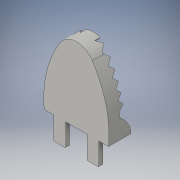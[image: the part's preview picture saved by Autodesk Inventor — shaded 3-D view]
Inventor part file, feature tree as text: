
AUTODESK INVENTOR PART (.ipt)
format: ipt  version: 2016 (Build 200138000, 138)  size: 525,824 bytes
history: native  units: in
note: dims shown in document units (in); Inventor stores cm internally (conversion verified against a paired STEP export)
features: sketch x25, extrude x24, other x12, plane x12, projected_geometry x8, reference x4, fillet x3
ambient origin geometry x8: Origin, YZ Plane, XZ Plane, XY Plane, X Axis, Y Axis, Z Axis, Center Point
bodies: Solid1 (feature_tree)
feature tree (88):
  extrude  "Extrusion1"  Depth=1.0in
  extrude  "Extrusion2"  Depth=0.3937in TaperAngle=0.0deg
  extrude  "Extrusion3"  Depth=1.0in
  extrude  "Extrusion4"  Depth=1.0in TaperAngle=0.0deg
  sketch  "Sketch5"  dims[d12=1.0in d13=0.0in d15=0.5in]
  other  "Work Point1"
  other  "Work Point2"
  other  "Work Point3"
  other  "Work Point4"
  other  "Work Point5"
  other  "Work Point6"
  other  "Work Point7"
  other  "Work Point8"
  other  "Work Point9"
  other  "Work Point10"
  other  "Work Point11"
  other  "Work Point12"
  plane  "Work Plane1"
  plane  "Work Plane2"
  plane  "Work Plane3"
  plane  "Work Plane4"
  plane  "Work Plane5"
  plane  "Work Plane6"
  sketch  "Sketch6"  dims[d16=2.3622in d18=0.45in d19=0.3937in d21=1.0in d23=0.25in]
  sketch  "Sketch7"  dims[d24=0.5in d25=0.25in]
  sketch  "Sketch8"  dims[d26=0.25in d27=0.5in d28=0.25in d29=0.25in d30=0.5in d31=0.25in]
  sketch  "Sketch9"  dims[d32=0.25in d33=0.5in d34=0.25in d35=0.25in d36=0.5in d37=0.25in]
  sketch  "Sketch10"  dims[d38=0.25in d39=0.5in d40=0.25in d44=1.0in d45=0.0in]
  sketch  "Sketch11"  dims[d46=1.0in d47=0.0in d48=1.0in d49=0.0in]
  extrude  "Extrusion5"  Depth=0.5in
  extrude  "Extrusion6"  Depth=0.3937in
  extrude  "Extrusion7"  Depth=0.25in
  extrude  "Extrusion8"  Depth=0.25in
  extrude  "Extrusion9"  Depth=0.25in
  extrude  "Extrusion10"  Depth=1.0in TaperAngle=0.0deg
  plane  "Work Plane7"
  plane  "Work Plane8"
  plane  "Work Plane9"
  plane  "Work Plane10"
  plane  "Work Plane11"
  plane  "Work Plane12"
  sketch  "Sketch13"  dims[d50=1.0in d51=0.0in d52=1.0in d53=0.0in]
  sketch  "Sketch14"  dims[d54=1.0in d55=0.0in d56=0.25in]
  sketch  "Sketch15"  dims[d57=0.5in d58=0.25in]
  sketch  "Sketch16"  dims[d59=0.25in d60=0.5in d61=0.25in d62=0.25in d63=0.5in d64=0.25in]
  sketch  "Sketch17"  dims[d65=0.25in d66=0.5in d67=0.25in d68=0.25in d69=0.5in d70=0.25in]
  sketch  "Sketch18"  dims[d71=0.25in d72=0.5in d73=0.25in d74=1.0in d75=0.0in]
  extrude  "Extrusion11"  Depth=1.0in TaperAngle=0.0deg
  extrude  "Extrusion12"  Depth=1.0in TaperAngle=0.0deg
  extrude  "Extrusion13"  Depth=0.25in
  extrude  "Extrusion14"  Depth=0.25in
  extrude  "Extrusion15"  Depth=0.25in
  extrude  "Extrusion16"  Depth=0.25in
  extrude  "Extrusion17"  Depth=1.0in TaperAngle=0.0deg
  extrude  "Extrusion18"  Depth=1.0in TaperAngle=0.0deg
  extrude  "Extrusion19"  Depth=1.0in TaperAngle=0.0deg
  extrude  "Extrusion20"  Depth=1.0in TaperAngle=0.0deg
  extrude  "Extrusion21"  Depth=0.3937in
  extrude  "Extrusion22"  Depth=0.3937in
  extrude  "Extrusion23"  Depth=0.1969in
  extrude  "Extrusion24"  Depth=0.1969in
  fillet  "Fillet1"  Radius=0.7874in
  fillet  "Fillet2"  Radius=1.2402in
  fillet  "Fillet3"  Radius=0.1969in
  sketch  "Sketch1"  dims[d0=4.5in d1=1.0in]
  reference  "Reference1"
  sketch  "Sketch2"  dims[d2=0.1969in d3=0.0in d4=0.3937in d5=0.0in]
  projected_geometry  "Projected Loop1"
  sketch  "Sketch3"  dims[d6=0.9843in d7=1.0in]
  sketch  "Sketch4"  dims[d8=4.0in d9=0.0in d10=1.0in d11=0.0in]
  projected_geometry  "Projected Loop2"
  projected_geometry  "Projected Loop3"
  sketch  "Sketch19"  dims[d76=1.0in d77=0.0in d78=1.0in d79=0.0in]
  projected_geometry  "Projected Loop4"
  sketch  "Sketch20"  dims[d80=1.0in d81=0.0in d82=1.0in d83=0.0in]
  reference  "Reference2"
  sketch  "Sketch21"  dims[d84=1.0in d85=0.0in d86=1.0in d87=0.0in]
  reference  "Reference3"
  reference  "Reference4"
  sketch  "Sketch22"  dims[d88=4.0in d89=0.0in d90=0.3937in]
  sketch  "Sketch23"  dims[d91=0.3937in d92=0.0787in]
  projected_geometry  "Projected Loop5"
  projected_geometry  "Projected Loop6"
  projected_geometry  "Projected Loop7"
  sketch  "Sketch24"  dims[d93=0.0787in d94=0.1969in]
  projected_geometry  "Projected Loop8"
  sketch  "Sketch25"  dims[d95=0.7874in d96=0.1969in d97=0.7874in d98=1.2402in d99=0.0in d100=0.1969in]
  sketch  "Sketch26"  dims[d101=0.1378in d102=1.5748in d103=0.0in d104=1.5748in d105=0.0in d106=0.2953in d107=0.0in d108=0.2in d109=0.0in d110=0.0098in d111=1.1972in d112=0.6262in d113=0.0098in d114=0.15in d115=0.1in d116=0.0in d117=0.0394in d118=0.0394in d119=0.0394in]
